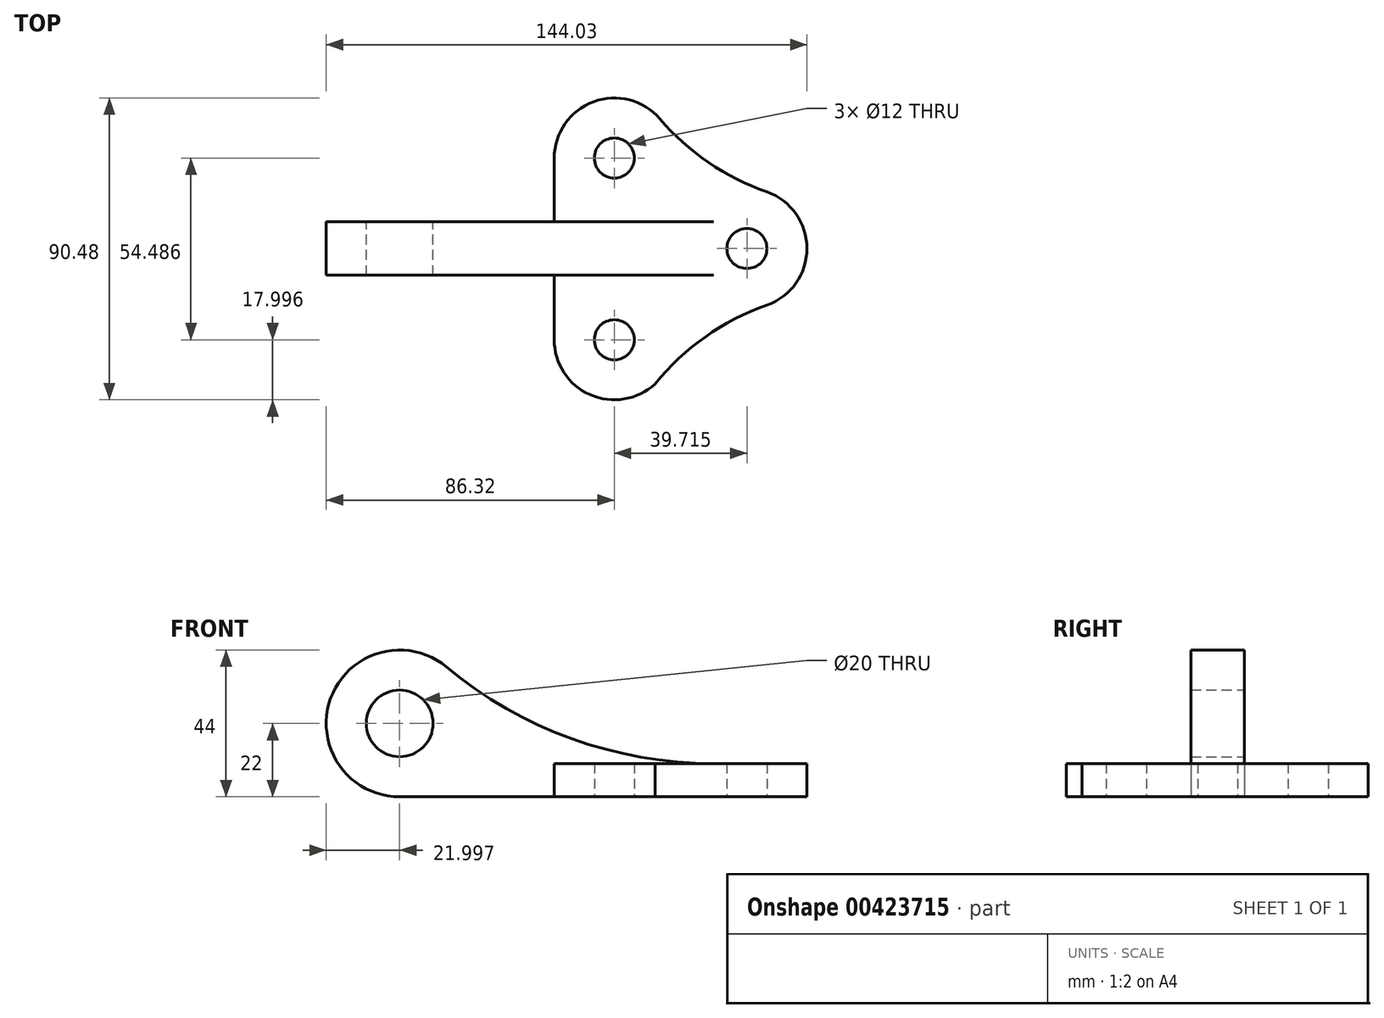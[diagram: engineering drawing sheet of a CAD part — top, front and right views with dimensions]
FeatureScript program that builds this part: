
annotation { "Feature Type Name" : "Feature", "Feature Type Description" : "" }
export const myFeature = defineFeature(function(context is Context, id is Id, definition is map)
    precondition{}
    {
        {
            var Q0;
            Q0=qCreatedBy(makeId("Top.planeOp"),FACE);
            var sketch = newSketch(context, id + "F0", { "sketchPlane" : qUnion([Q0])});
            skCircle(sketch, "E0", {"center": v(0, 27.12) * mm, "radius": 6 * mm});
            skCircle(sketch, "E1", {"center": v(0, -27.36) * mm, "radius": 6 * mm});
            skCircle(sketch, "E2", {"center": v(39.71, 0) * mm, "radius": 6 * mm});
            skArc(sketch, "E3", {"start": v(13.65, 38.86) * mm, "mid": v(-6.26, 44) * mm, "end": v(-18, 27.12) * mm});
            skArc(sketch, "E4", {"start": v(45.68, -16.98) * mm, "mid": v(57.71, 0) * mm, "end": v(45.68, 16.98) * mm});
            skArc(sketch, "E5", {"start": v(-18, -27.36) * mm, "mid": v(-5.23, -44.59) * mm, "end": v(14.97, -37.37) * mm});
            skArc(sketch, "E6", {"start": v(13.65, 38.86) * mm, "mid": v(28.23, 25.81) * mm, "end": v(45.68, 16.98) * mm});
            skArc(sketch, "E7.MirrorC", {"start": v(12.19, -40.61) * mm, "mid": v(27.29, -26.47) * mm, "end": v(45.68, -16.98) * mm});
            skLineSegment(sketch, "E8", {"start": v(-18, 27.12) * mm, "end": v(-18, -27.36) * mm});
            skSolve(sketch);
        }
        {
            var Q0;
            Q0=makeQuery(id+"F0.imprint","IMPRINT",FACE,{"disambiguationData":[TD([[makeQuery(id+"F0.imprint","IMPRINT",EDGE,{"derivedFrom":sQuery(id+"F0.wireOp",EDGE,"E0")}),-1.0]])]});
            extrude(context, id + "F1", {"entities" : qUnion([Q0]), "depth" : 10 * mm});
        }
        {
            var Q0;
            Q0=qCreatedBy(makeId("Front.planeOp"),FACE);
            var sketch = newSketch(context, id + "F2", { "sketchPlane" : qUnion([Q0])});
            skLineSegment(sketch, "E9", {"start": v(0, 0) * mm, "end": v(-64.32, 0) * mm});
            skLineSegment(sketch, "E10", {"start": v(-64.32, 0) * mm, "end": v(-64.32, 39.25) * mm, "construction": true});
            skCircle(sketch, "E11", {"center": v(-64.32, 22) * mm, "radius": 10 * mm});
            skArc(sketch, "E12", {"start": v(-50.25, 38.91) * mm, "mid": v(-85.01, 29.48) * mm, "end": v(-64.32, 0) * mm});
            skArc(sketch, "E13", {"start": v(-50.25, 38.91) * mm, "mid": v(-12.8, 17.45) * mm, "end": v(29.7, 10) * mm});
            skLineSegment(sketch, "E14", {"start": v(29.7, 10) * mm, "end": v(29.7, 0) * mm});
            skLineSegment(sketch, "E15", {"start": v(29.7, 0) * mm, "end": v(0, 0) * mm});
            skSolve(sketch);
        }
        {
            var Q0;
            Q0=makeQuery(id+"F2.imprint","IMPRINT",FACE,{"disambiguationData":[TD([[makeQuery(id+"F2.imprint","IMPRINT",EDGE,{"derivedFrom":sQuery(id+"F2.wireOp",EDGE,"E9")}),-1.0]])]});
            extrude(context, id + "F3", {"entities" : qUnion([Q0]), "operationType" : NewBodyOperationType.ADD, "endBound" : BoundingType.SYMMETRIC, "depth" : 16 * mm});
        }
    });
